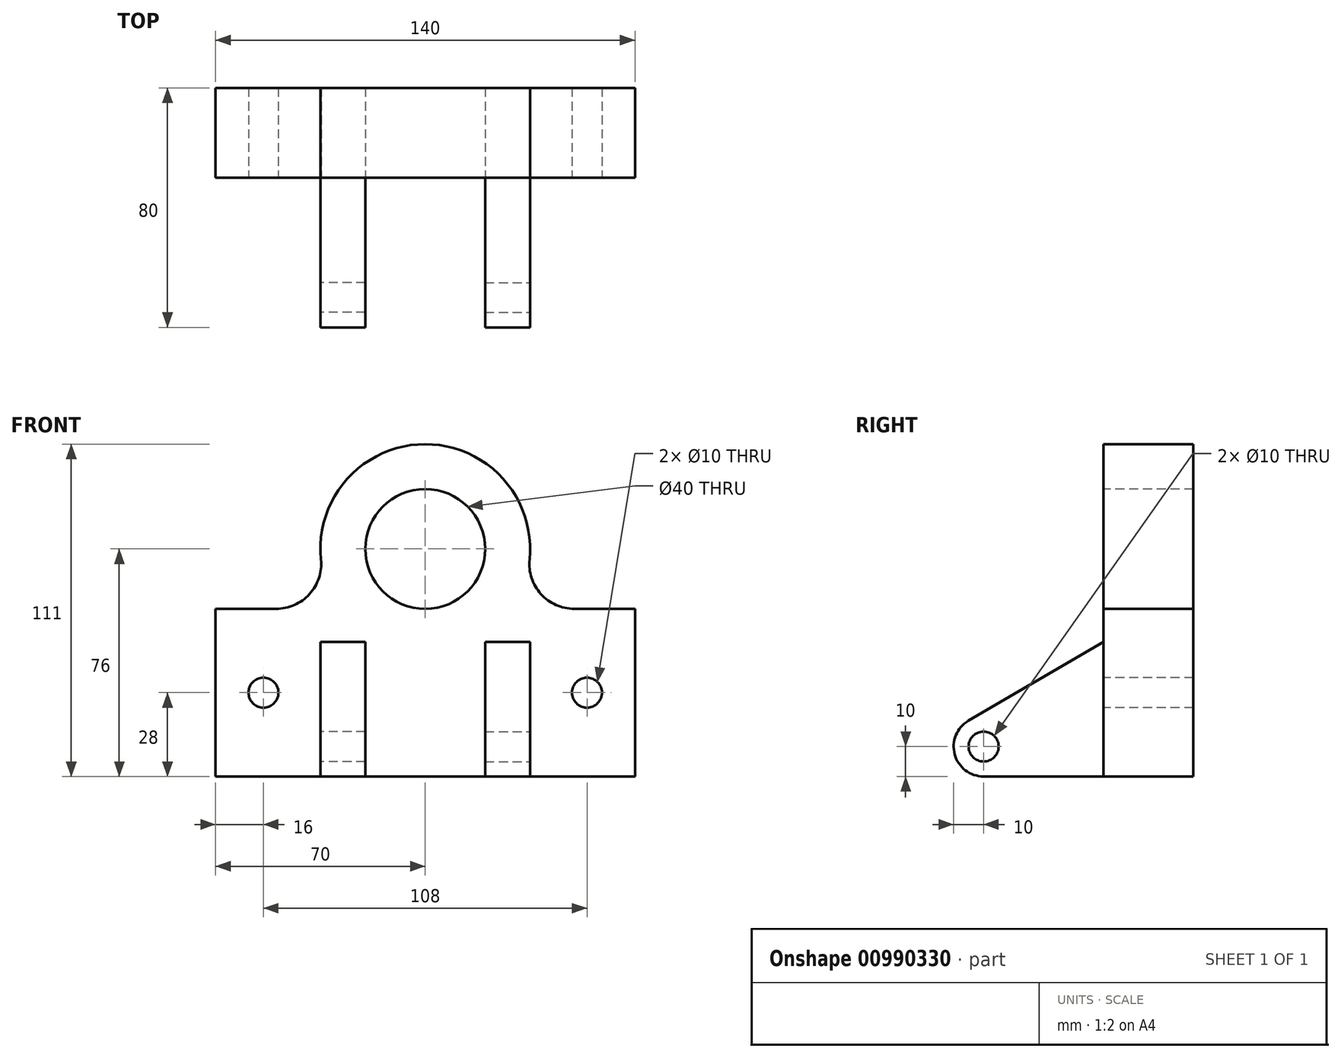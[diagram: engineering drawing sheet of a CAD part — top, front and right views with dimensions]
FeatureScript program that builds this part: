
annotation { "Feature Type Name" : "Feature", "Feature Type Description" : "" }
export const myFeature = defineFeature(function(context is Context, id is Id, definition is map)
    precondition{}
    {
        {
            var Q0;
            Q0=qCreatedBy(makeId("Front.planeOp"),FACE);
            var sketch = newSketch(context, id + "F0", { "sketchPlane" : qUnion([Q0])});
            skLineSegment(sketch, "E0", {"start": v(-70, 0) * mm, "end": v(0, 0) * mm});
            skLineSegment(sketch, "E1.MirrorCS", {"start": v(70, 0) * mm, "end": v(0, 0) * mm});
            skLineSegment(sketch, "E2", {"start": v(-70, 0) * mm, "end": v(-70, -56) * mm});
            skLineSegment(sketch, "E3.MirrorCS", {"start": v(70, 0) * mm, "end": v(70, -56) * mm});
            skLineSegment(sketch, "E4", {"start": v(-70, -56) * mm, "end": v(70, -56) * mm});
            skLineSegment(sketch, "E5", {"start": v(-70, -56) * mm, "end": v(-54, -56) * mm, "construction": true});
            skLineSegment(sketch, "E6", {"start": v(-54, -56) * mm, "end": v(-35, -56) * mm, "construction": true});
            skLineSegment(sketch, "E7", {"start": v(-70, -56) * mm, "end": v(-70, -28) * mm, "construction": true});
            skLineSegment(sketch, "E8", {"start": v(-70, -56) * mm, "end": v(-70, -11) * mm, "construction": true});
            skLineSegment(sketch, "E9", {"start": v(-70, -28) * mm, "end": v(70, -28) * mm, "construction": true});
            skLineSegment(sketch, "E10", {"start": v(-70, -11) * mm, "end": v(70, -11) * mm, "construction": true});
            skLineSegment(sketch, "E11", {"start": v(-54, -56) * mm, "end": v(-54, -11) * mm, "construction": true});
            skLineSegment(sketch, "E12", {"start": v(-35, -56) * mm, "end": v(-35, -11) * mm, "construction": true});
            skCircle(sketch, "E13", {"center": v(-54, -28) * mm, "radius": 5 * mm});
            skLineSegment(sketch, "E14", {"start": v(0, 0) * mm, "end": v(0, 20) * mm, "construction": true});
            skCircle(sketch, "E15", {"center": v(0, 20) * mm, "radius": 20 * mm});
            skArc(sketch, "E16", {"start": v(28.72, 0) * mm, "mid": v(0, 55) * mm, "end": v(-28.72, 0) * mm});
            skCircle(sketch, "E17.MirrorC", {"center": v(54, -28) * mm, "radius": 5 * mm});
            skSolve(sketch);
        }
        {
            var Q0;
            Q0=qCreatedBy(makeId("Right.planeOp"),FACE);
            var Q1;
            Q1=sQuery(id+"F0.wireOp",VERTEX,"E12.end");
            cPlane(context, id + "F1", {"entities" : qUnion([Q0, Q1]), "cplaneType" : CPlaneType.PLANE_POINT, "offset" : 25 * mm, "width" : 150 * mm, "height" : 150 * mm});
        }
        {
            var Q0;
            Q0=qCreatedBy(id+"F1.planeOp",FACE);
            var sketch = newSketch(context, id + "F2", { "sketchPlane" : qUnion([Q0])});
            skLineSegment(sketch, "E18", {"start": v(0, 0) * mm, "end": v(0, -56) * mm});
            skLineSegment(sketch, "E19", {"start": v(0, -56) * mm, "end": v(-40, -56) * mm});
            skArc(sketch, "E20", {"start": v(-40, -56) * mm, "mid": v(-49.65, -48.62) * mm, "end": v(-45.05, -37.37) * mm});
            skLineSegment(sketch, "E21", {"start": v(0, -56) * mm, "end": v(0, -11) * mm, "construction": true});
            skLineSegment(sketch, "E22", {"start": v(0, -11) * mm, "end": v(-45.05, -37.37) * mm});
            skCircle(sketch, "E23", {"center": v(-40, -46) * mm, "radius": 5 * mm});
            skSolve(sketch);
        }
        {
            var Q0;
            {var subQ0=sQuery(id+"F0.wireOp",EDGE,"E15");Q0=makeQuery(id+"F0.imprint","IMPRINT",FACE,{"disambiguationData":[TD([[makeQuery(id+"F0.imprint","IMPRINT",EDGE,{"derivedFrom":subQ0}),-1.0]])]});}
            var Q1;
            {var subQ7=sQuery(id+"F0.wireOp",EDGE,"E2");Q1=makeQuery(id+"F0.imprint","IMPRINT",FACE,{"disambiguationData":[TD([[makeQuery(id+"F0.imprint","IMPRINT",EDGE,{"derivedFrom":subQ7}),1.0]])]});}
            extrude(context, id + "F3", {"entities" : qUnion([Q0, Q1]), "oppositeDirection" : true, "depth" : 30 * mm, "offsetDistance" : 25 * mm});
        }
        {
            var Q0;
            Q0=makeQuery(id+"F3.opExtrude","SWEPT_EDGE",EDGE,{"disambiguationData":[OSD([sQuery(id+"F0.wireOp",EDGE,"E0"),sQuery(id+"F0.wireOp",EDGE,"E16")])]});
            var Q1;
            Q1=makeQuery(id+"F3.opExtrude","SWEPT_EDGE",EDGE,{"disambiguationData":[OSD([sQuery(id+"F0.wireOp",EDGE,"E1.MirrorCS"),sQuery(id+"F0.wireOp",EDGE,"E16")])]});
            fillet(context, id + "F4", {"entities" : qUnion([Q0, Q1]), "radius" : 15 * mm, "tangentPropagation" : true, "allowEdgeOverflow" : false});
        }
        {
            var Q0;
            {var subQ1=sQuery(id+"F2.wireOp",EDGE,"E19");Q0=makeQuery(id+"F2.imprint","IMPRINT",FACE,{"disambiguationData":[TD([[makeQuery(id+"F2.imprint","IMPRINT",EDGE,{"derivedFrom":subQ1}),-1.0]])]});}
            extrude(context, id + "F5", {"entities" : qUnion([Q0]), "operationType" : NewBodyOperationType.ADD, "depth" : 15 * mm, "offsetDistance" : 25 * mm});
        }
        {
            var Q0;
            Q0=makeQuery(id+"F3.opExtrude","SWEPT_BODY",BODY,{"disambiguationData":[OSD([sQuery(id+"F0.wireOp",EDGE,"E0"),sQuery(id+"F0.wireOp",EDGE,"E1.MirrorCS"),sQuery(id+"F0.wireOp",EDGE,"E2"),sQuery(id+"F0.wireOp",EDGE,"E3.MirrorCS"),sQuery(id+"F0.wireOp",EDGE,"E4"),sQuery(id+"F0.wireOp",EDGE,"E13"),sQuery(id+"F0.wireOp",EDGE,"E15"),sQuery(id+"F0.wireOp",EDGE,"E16"),sQuery(id+"F0.wireOp",EDGE,"E17.MirrorC")])]});
            var Q1;
            Q1=qCreatedBy(makeId("Right.planeOp"),FACE);
            mirror(context, id + "F6", {"operationType" : NewBodyOperationType.ADD, "entities" : qUnion([Q0]), "mirrorPlane" : qUnion([Q1])});
        }
    });
